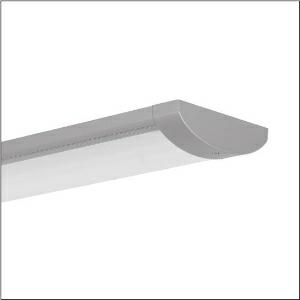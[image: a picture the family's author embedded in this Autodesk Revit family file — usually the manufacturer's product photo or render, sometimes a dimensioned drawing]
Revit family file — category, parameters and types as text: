
# Revit family: tv_20_5xa861d4n0x
name_source: partatom
category: Lighting Fixtures
units: mm (PartAtom-declared; Revit-internal decimal feet)

## family parameters
Cut with Voids When Loaded = No
Host = Face
Light Source = No
Part Type = Normal
Room Calculation Point = No
Round Connector Dimension = Use Diameter
Shared = No

## types (1)
- TV 20 (1 x LED 4000K / CRI = 80 (unbekannt), 5120 lm, 4000K)
    Apparent Load = 50 VA
    CIE Flux Codes = 48 78 95 99 100
    Color Rendering = 80
    Color Temperature = 4000K
    Default Elevation = 1800 mm
    Description = TV 20, vandal-proof luminaire, primary light control with specular reflector, of aluminium, matt, primary optical cover: enclosure, of PC, frosted, light emission: direct distribution, primary light characteristic: symmetric, installation type: surface-mounted, LED, rated luminous flux: 5.120lm, luminous efficacy: 102lm/W, light colour: 840, colour temperature: 4000K, control gear: DALI, mains connection: 230V, AC, 50Hz, rated input power: 50W, luminaire housing, of aluminium, coated, Siteco® metallic grey (DB 702S), with wall and ceiling fixing element, length: 1.561mm, width: 260mm, height: 70mm, mounting height: 2.5..4.0m, protection rating (complete): IP65, insulation class (complete): insulation class I (protective earthing), certification: CE, protection symbol: F, impact resistance: 2x IK10, standard: EN 60598, packaging unit: 1 piece
    Height = 70 mm
    Lamp = 1 x LED 4000K / CRI >= 80 (unbekannt)
    Lamp Light Flux = 5120 lm
    Lamp count = 1
    Length = 1561 mm
    Luminous efficacy = 102 lm/W
    Manufacturer = Siteco
    ModVariant = No
    Model = 5XA861D4N0X
    Mounting Place = Ceiling
    Mounting Type = Surface mounted
    Number of Poles = 1
    OnlyDefault = Yes
    Power Factor = 1
    Product Name = TV 20
    Product group = vandal-proof luminaire
    ProductGroupID = 310
    Protection Class = Protection class I
    Protection Degree = IP 65
    RLX_Detail_Level = 1
    RLX_Emergency_Light_Flux = 0 lm
    RLX_Emergency_Type = 0
    RLX_Emergency_Type_DB = No
    RlxData = <blob elided: 25221 chars, md5=5e53f25d>
    Socket = socket
    Standby Power = 0 W
    System Light Flux = 5120 lm
    System Power = 50 W
    Type Comments = Product without accessories
    Type Image = l_1004809.jpg
    URL = http://relux.com
    VarID = ---
    Voltage = 0 V
    Weight = 0.00 kg
    Width = 260 mm

## geometry (parser evidence)
native form markers: Blend x4, Sweep x10
no freeform markers — native parametric forms only
